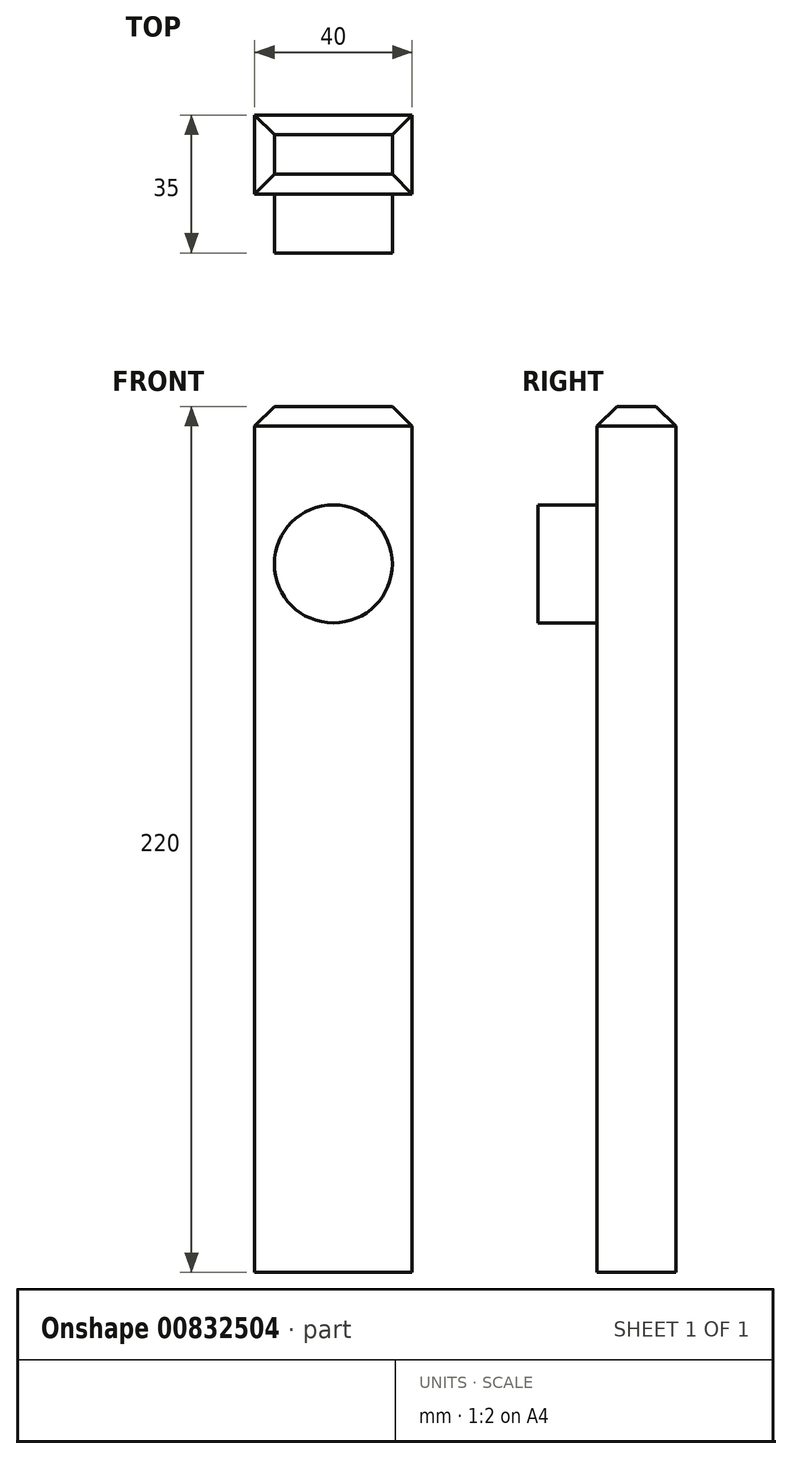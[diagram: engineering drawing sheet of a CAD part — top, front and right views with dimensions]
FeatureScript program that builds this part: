
annotation { "Feature Type Name" : "Feature", "Feature Type Description" : "" }
export const myFeature = defineFeature(function(context is Context, id is Id, definition is map)
    precondition{}
    {
        {
            var Q0;
            Q0=qCreatedBy(makeId("Top.planeOp"),FACE);
            var sketch = newSketch(context, id + "F0", { "sketchPlane" : qUnion([Q0])});
            skLineSegment(sketch, "E0.bottom", {"start": v(-20, 20) * mm, "end": v(20, 20) * mm});
            skLineSegment(sketch, "E0.top", {"start": v(-20, 0) * mm, "end": v(20, 0) * mm});
            skLineSegment(sketch, "E0.left", {"start": v(-20, 20) * mm, "end": v(-20, 0) * mm});
            skLineSegment(sketch, "E0.right", {"start": v(20, 20) * mm, "end": v(20, 0) * mm});
            skSolve(sketch);
        }
        {
            var Q0;
            Q0=makeQuery(id+"F0.imprint","IMPRINT",FACE,{"disambiguationData":[TD([[makeQuery(id+"F0.imprint","IMPRINT",EDGE,{"derivedFrom":sQuery(id+"F0.wireOp",EDGE,"E0.bottom")}),-1.0]])]});
            extrude(context, id + "F1", {"entities" : qUnion([Q0]), "depth" : 120 * mm, "offsetDistance" : 25 * mm, "hasSecondDirection" : true, "secondDirectionOppositeDirection" : true, "secondDirectionDepth" : 100 * mm});
        }
        {
            var Q0;
            Q0=makeQuery(id+"F1.opExtrude","SWEPT_FACE",FACE,{"disambiguationData":[OSD([sQuery(id+"F0.wireOp",EDGE,"E0.top")])]});
            var sketch = newSketch(context, id + "F2", { "sketchPlane" : qUnion([Q0])});
            skCircle(sketch, "E1", {"center": v(0, 80) * mm, "radius": 15 * mm});
            skSolve(sketch);
        }
        {
            var Q0;
            Q0=makeQuery(id+"F2.imprint","IMPRINT",FACE,{"disambiguationData":[TD([[makeQuery(id+"F2.imprint","IMPRINT",EDGE,{"derivedFrom":sQuery(id+"F2.wireOp",EDGE,"E1")}),1.0]])]});
            extrude(context, id + "F3", {"entities" : qUnion([Q0]), "operationType" : NewBodyOperationType.ADD, "depth" : 15 * mm, "offsetDistance" : 25 * mm});
        }
        {
            var Q0;
            Q0=makeQuery(id+"F1.opExtrude","CAP_EDGE",EDGE,{"disambiguationData":[OSD([sQuery(id+"F0.wireOp",EDGE,"E0.top")])],"isStart":false});
            var Q1;
            Q1=makeQuery(id+"F1.opExtrude","CAP_EDGE",EDGE,{"disambiguationData":[OSD([sQuery(id+"F0.wireOp",EDGE,"E0.right")])],"isStart":false});
            var Q2;
            Q2=makeQuery(id+"F1.opExtrude","CAP_EDGE",EDGE,{"disambiguationData":[OSD([sQuery(id+"F0.wireOp",EDGE,"E0.bottom")])],"isStart":false});
            var Q3;
            Q3=makeQuery(id+"F1.opExtrude","CAP_EDGE",EDGE,{"disambiguationData":[OSD([sQuery(id+"F0.wireOp",EDGE,"E0.left")])],"isStart":false});
            chamfer(context, id + "F4", {"entities" : qUnion([Q0, Q1, Q2, Q3]), "width" : 5 * mm, "tangentPropagation" : true});
        }
    });
